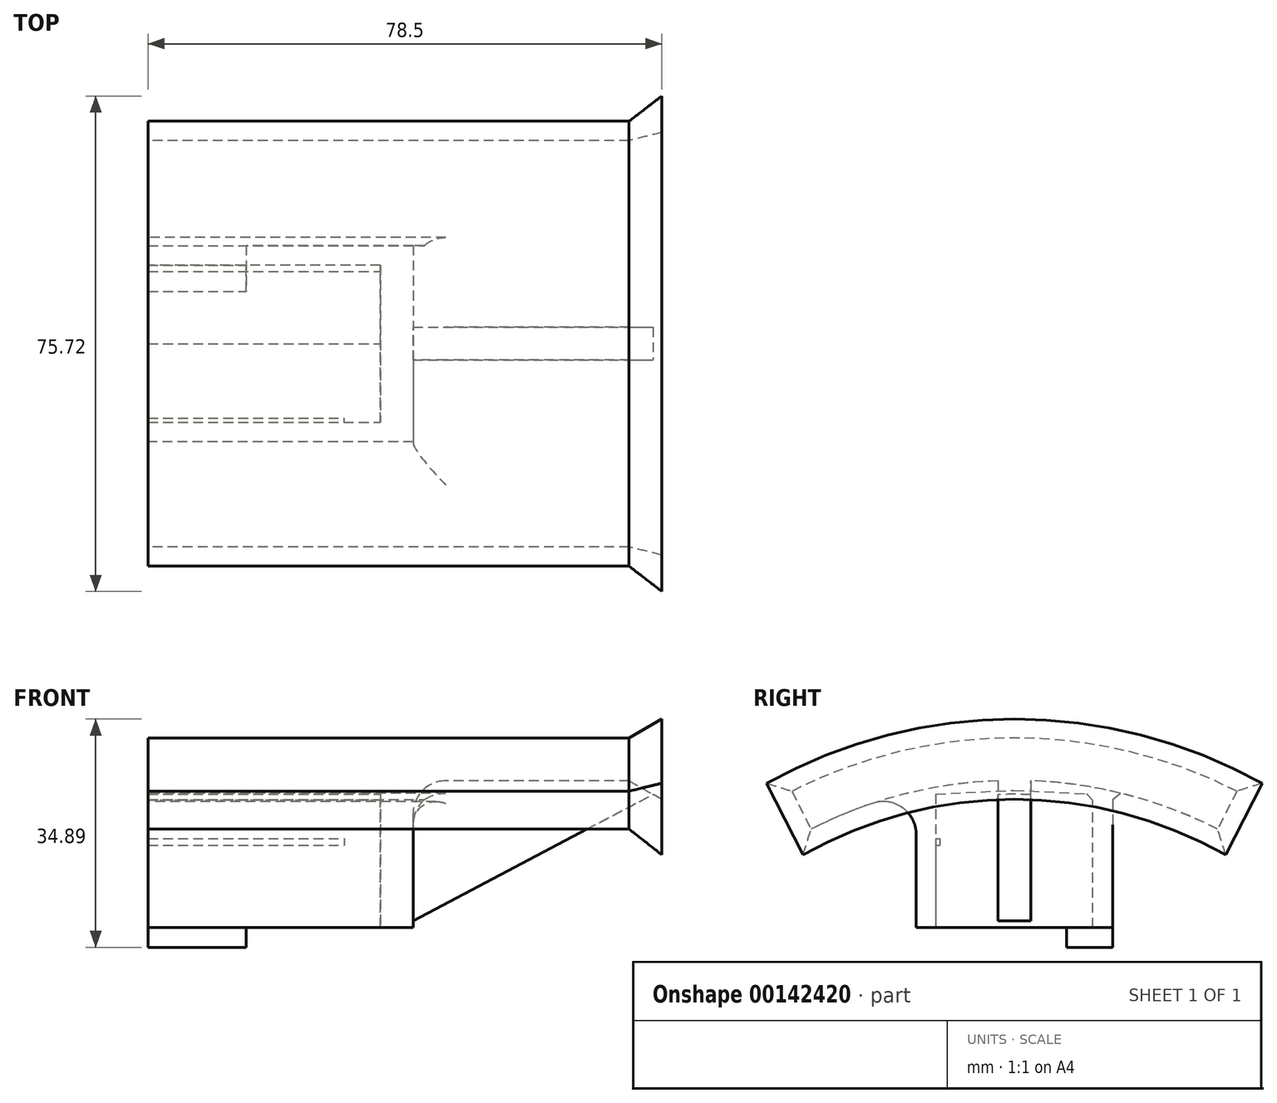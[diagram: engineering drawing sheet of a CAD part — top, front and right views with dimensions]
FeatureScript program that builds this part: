
annotation { "Feature Type Name" : "Feature", "Feature Type Description" : "" }
export const myFeature = defineFeature(function(context is Context, id is Id, definition is map)
    precondition{}
    {
        {
            var Q0;
            Q0=qCreatedBy(makeId("Right.planeOp"),FACE);
            var sketch = newSketch(context, id + "F0", { "sketchPlane" : qUnion([Q0])});
            skLineSegment(sketch, "E0", {"start": v(0, 0) * mm, "end": v(0, -27) * mm});
            skLineSegment(sketch, "E1", {"start": v(0, -27) * mm, "end": v(-7, -27) * mm});
            skLineSegment(sketch, "E2", {"start": v(-7, -27) * mm, "end": v(-7, -24) * mm});
            skLineSegment(sketch, "E3", {"start": v(-7, -24) * mm, "end": v(-3, -24) * mm});
            skLineSegment(sketch, "E4", {"start": v(-3, -24) * mm, "end": v(-3, -3) * mm});
            skLineSegment(sketch, "E5", {"start": v(-3, -3) * mm, "end": v(-27, -3) * mm});
            skLineSegment(sketch, "E6", {"start": v(-27, -3) * mm, "end": v(-27, -24) * mm});
            skLineSegment(sketch, "E7", {"start": v(-27, -24) * mm, "end": v(-30, -24) * mm});
            skLineSegment(sketch, "E8", {"start": v(-30, -24) * mm, "end": v(-30, 0) * mm});
            skLineSegment(sketch, "E9", {"start": v(-30, 0) * mm, "end": v(0, 0) * mm});
            skLineSegment(sketch, "E10.bottom", {"start": v(-27, -10.4) * mm, "end": v(-26.4, -10.4) * mm});
            skLineSegment(sketch, "E10.top", {"start": v(-27, -11.4) * mm, "end": v(-26.4, -11.4) * mm});
            skLineSegment(sketch, "E10.left", {"start": v(-27, -10.4) * mm, "end": v(-27, -11.4) * mm});
            skLineSegment(sketch, "E10.right", {"start": v(-26.4, -10.4) * mm, "end": v(-26.4, -11.4) * mm});
            skLineSegment(sketch, "E11", {"start": v(-3, -24) * mm, "end": v(0, -24) * mm});
            skLineSegment(sketch, "E12", {"start": v(-27, -3.6) * mm, "end": v(-15, -3) * mm});
            skLineSegment(sketch, "E13", {"start": v(-15, -3) * mm, "end": v(-3, -3.6) * mm});
            skSolve(sketch);
        }
        {
            var Q0;
            Q0=makeQuery(id+"F0.imprint","IMPRINT",FACE,{"disambiguationData":[TD([[makeQuery(id+"F0.imprint","IMPRINT",EDGE,{"derivedFrom":sQuery(id+"F0.wireOp",EDGE,"E0")}),-1.0]])]});
            var Q1;
            Q1=makeQuery(id+"F0.imprint","IMPRINT",FACE,{"disambiguationData":[TD([[makeQuery(id+"F0.imprint","IMPRINT",EDGE,{"derivedFrom":sQuery(id+"F0.wireOp",EDGE,"E10.bottom")}),-1.0]])]});
            var Q2;
            Q2=makeQuery(id+"F0.imprint","IMPRINT",FACE,{"disambiguationData":[TD([[makeQuery(id+"F0.imprint","IMPRINT",EDGE,{"derivedFrom":sQuery(id+"F0.wireOp",EDGE,"E4")}),-1.0]])]});
            var Q3;
            {var subQ3=sQuery(id+"F0.wireOp",EDGE,"E13");Q3=makeQuery(id+"F0.imprint","IMPRINT",FACE,{"disambiguationData":[TD([[makeQuery(id+"F0.imprint","IMPRINT",EDGE,{"derivedFrom":subQ3}),1.0]])]});}
            var Q4;
            {var subQ3=sQuery(id+"F0.wireOp",EDGE,"E12");Q4=makeQuery(id+"F0.imprint","IMPRINT",FACE,{"disambiguationData":[TD([[makeQuery(id+"F0.imprint","IMPRINT",EDGE,{"derivedFrom":subQ3}),1.0]])]});}
            extrude(context, id + "F1", {"entities" : qUnion([Q0, Q1, Q2, Q3, Q4]), "oppositeDirection" : true, "depth" : 15 * mm});
        }
        {
            var Q0;
            Q0=makeQuery(id+"F1.opExtrude","CAP_FACE",FACE,{"disambiguationData":[OSD([sQuery(id+"F0.wireOp",EDGE,"E0"),sQuery(id+"F0.wireOp",EDGE,"E1"),sQuery(id+"F0.wireOp",EDGE,"E2"),sQuery(id+"F0.wireOp",EDGE,"E3"),sQuery(id+"F0.wireOp",EDGE,"E4"),sQuery(id+"F0.wireOp",EDGE,"E5"),sQuery(id+"F0.wireOp",EDGE,"E6"),sQuery(id+"F0.wireOp",EDGE,"E7"),sQuery(id+"F0.wireOp",EDGE,"E8"),sQuery(id+"F0.wireOp",EDGE,"E9"),sQuery(id+"F0.wireOp",EDGE,"E10.bottom"),sQuery(id+"F0.wireOp",EDGE,"E10.top"),sQuery(id+"F0.wireOp",EDGE,"E10.right")])],"isStart":true});
            var sketch = newSketch(context, id + "F2", { "sketchPlane" : qUnion([Q0])});
            skLineSegment(sketch, "E14.bottom", {"start": v(-30, 0) * mm, "end": v(-27, 0) * mm});
            skLineSegment(sketch, "E14.top", {"start": v(-30, -24) * mm, "end": v(-27, -24) * mm});
            skLineSegment(sketch, "E14.left", {"start": v(-30, 0) * mm, "end": v(-30, -24) * mm});
            skLineSegment(sketch, "E14.right", {"start": v(-27, 0) * mm, "end": v(-27, -24) * mm});
            skLineSegment(sketch, "E15.bottom", {"start": v(0, 0) * mm, "end": v(-27, 0) * mm});
            skLineSegment(sketch, "E15.top", {"start": v(0, -24) * mm, "end": v(-27, -24) * mm});
            skLineSegment(sketch, "E15.left", {"start": v(0, 0) * mm, "end": v(0, -24) * mm});
            skLineSegment(sketch, "E16.bottom", {"start": v(0, -24) * mm, "end": v(-3, -24) * mm});
            skLineSegment(sketch, "E16.top", {"start": v(0, -24) * mm, "end": v(-3, -24) * mm});
            skLineSegment(sketch, "E16.left", {"start": v(0, -24) * mm, "end": v(0, -24) * mm});
            skLineSegment(sketch, "E16.right", {"start": v(-3, -24) * mm, "end": v(-3, -24) * mm});
            skSolve(sketch);
        }
        {
            var Q0;
            Q0=makeQuery(id+"F2.imprint","IMPRINT",FACE,{"disambiguationData":[TD([[makeQuery(id+"F2.imprint","IMPRINT",EDGE,{"derivedFrom":sQuery(id+"F2.wireOp",EDGE,"E14.bottom")}),-1.0]])]});
            var Q1;
            Q1=makeQuery(id+"F2.imprint","IMPRINT",FACE,{"disambiguationData":[TD([[makeQuery(id+"F2.imprint","IMPRINT",EDGE,{"derivedFrom":sQuery(id+"F2.wireOp",EDGE,"E15.bottom")}),-1.0]])]});
            extrude(context, id + "F3", {"entities" : qUnion([Q0, Q1]), "operationType" : NewBodyOperationType.ADD, "depth" : 20.5 * mm});
        }
        {
            var Q0;
            Q0=makeQuery(id+"F3.opExtrude","CAP_FACE",FACE,{"disambiguationData":[OSD([sQuery(id+"F2.wireOp",EDGE,"E14.bottom"),sQuery(id+"F2.wireOp",EDGE,"E14.top"),sQuery(id+"F2.wireOp",EDGE,"E14.left"),sQuery(id+"F2.wireOp",EDGE,"E14.right"),sQuery(id+"F2.wireOp",EDGE,"E15.bottom"),sQuery(id+"F2.wireOp",EDGE,"E15.top"),sQuery(id+"F2.wireOp",EDGE,"E15.left"),sQuery(id+"F2.wireOp",EDGE,"E16.bottom")])],"isStart":false});
            var sketch = newSketch(context, id + "F4", { "sketchPlane" : qUnion([Q0])});
            skLineSegment(sketch, "E17.bottom", {"start": v(-30, 0) * mm, "end": v(0, 0) * mm});
            skLineSegment(sketch, "E17.top", {"start": v(-30, -24) * mm, "end": v(0, -24) * mm});
            skLineSegment(sketch, "E17.left", {"start": v(-30, 0) * mm, "end": v(-30, -24) * mm});
            skLineSegment(sketch, "E17.right", {"start": v(0, 0) * mm, "end": v(0, -24) * mm});
            skSolve(sketch);
        }
        {
            var Q0;
            Q0=qSketchRegion(id+"F4",true);
            extrude(context, id + "F5", {"entities" : qUnion([Q0]), "operationType" : NewBodyOperationType.ADD, "depth" : 5 * mm});
        }
        {
            var Q0;
            Q0=makeQuery(id+"F5.opExtrude","CAP_FACE",FACE,{"disambiguationData":[OSD([sQuery(id+"F4.wireOp",EDGE,"E17.bottom"),sQuery(id+"F4.wireOp",EDGE,"E17.top"),sQuery(id+"F4.wireOp",EDGE,"E17.left"),sQuery(id+"F4.wireOp",EDGE,"E17.right")])],"isStart":false});
            var sketch = newSketch(context, id + "F6", { "sketchPlane" : qUnion([Q0])});
            skCircle(sketch, "E18", {"center": v(-15, -70) * mm, "radius": 75 * mm});
            skCircle(sketch, "E19", {"center": v(-15, -70) * mm, "radius": 68.5 * mm});
            skLineSegment(sketch, "E20", {"start": v(-49, -3.15) * mm, "end": v(-15, -70) * mm});
            skLineSegment(sketch, "E21", {"start": v(19, -3.15) * mm, "end": v(-15, -70) * mm});
            skSolve(sketch);
        }
        {
            var Q0;
            {var subQ12=makeQuery(id+"F5.opExtrude","CAP_EDGE",EDGE,{"disambiguationData":[OSD([sQuery(id+"F4.wireOp",EDGE,"E17.bottom")])],"isStart":false});Q0=makeQuery(id+"F6.imprint","IMPRINT",FACE,{"disambiguationData":[TD([[makeQuery(id+"F6.imprint","IMPRINT",EDGE,{"derivedFrom":subQ12}),1.0]])]});}
            var Q1;
            {var subQ5=makeQuery(id+"F5.opExtrude","CAP_EDGE",EDGE,{"disambiguationData":[OSD([sQuery(id+"F4.wireOp",EDGE,"E17.bottom")])],"isStart":false});Q1=makeQuery(id+"F6.imprint","IMPRINT",FACE,{"disambiguationData":[TD([[makeQuery(id+"F6.imprint","IMPRINT",EDGE,{"derivedFrom":subQ5}),-1.0]])]});}
            var Q2;
            Q2=makeQuery(id+"F1.opExtrude","CAP_FACE",FACE,{"disambiguationData":[OSD([sQuery(id+"F0.wireOp",EDGE,"E0"),sQuery(id+"F0.wireOp",EDGE,"E1"),sQuery(id+"F0.wireOp",EDGE,"E2"),sQuery(id+"F0.wireOp",EDGE,"E3"),sQuery(id+"F0.wireOp",EDGE,"E4"),sQuery(id+"F0.wireOp",EDGE,"E5"),sQuery(id+"F0.wireOp",EDGE,"E6"),sQuery(id+"F0.wireOp",EDGE,"E7"),sQuery(id+"F0.wireOp",EDGE,"E8"),sQuery(id+"F0.wireOp",EDGE,"E9"),sQuery(id+"F0.wireOp",EDGE,"E10.bottom"),sQuery(id+"F0.wireOp",EDGE,"E10.top"),sQuery(id+"F0.wireOp",EDGE,"E10.right")])],"isStart":false});
            extrude(context, id + "F7", {"entities" : qUnion([Q0, Q1]), "operationType" : NewBodyOperationType.ADD, "depth" : 33 * mm, "hasSecondDirection" : true, "secondDirectionBound" : SecondDirectionBoundingType.UP_TO_SURFACE, "secondDirectionOppositeDirection" : true, "secondDirectionBoundEntityFace" : qUnion([Q2]), "secondDirectionDepth" : 25 * mm});
        }
        {
            var Q0;
            Q0=makeQuery(id+"F7.opExtrude","CAP_FACE",FACE,{"disambiguationData":[OSD([sQuery(id+"F6.wireOp",EDGE,"E18"),sQuery(id+"F6.wireOp",EDGE,"E19"),sQuery(id+"F6.wireOp",EDGE,"E20"),sQuery(id+"F6.wireOp",EDGE,"E21")])],"isStart":false});
            extrude(context, id + "F8", {"entities" : qUnion([Q0]), "operationType" : NewBodyOperationType.ADD, "depth" : 5 * mm, "hasDraft" : true, "draftAngle" : 30 * degree});
        }
        {
            var Q0;
            Q0=qCreatedBy(makeId("Front.planeOp"),FACE);
            var sketch = newSketch(context, id + "F9", { "sketchPlane" : qUnion([Q0])});
            skLineSegment(sketch, "E22", {"start": v(25.49, -22.98) * mm, "end": v(63.38, -2.98) * mm});
            skLineSegment(sketch, "E23", {"start": v(63.38, -2.98) * mm, "end": v(63.38, 0.02) * mm});
            skLineSegment(sketch, "E24", {"start": v(63.38, 0.02) * mm, "end": v(25.5, 0.02) * mm});
            skLineSegment(sketch, "E25", {"start": v(25.5, 0.02) * mm, "end": v(25.49, -22.98) * mm});
            skSolve(sketch);
        }
        {
            var Q0;
            Q0=qSketchRegion(id+"F9",true);
            extrude(context, id + "F10", {"entities" : qUnion([Q0]), "depth" : 5 * mm});
        }
        {
            var Q0;
            Q0=makeQuery(id+"F10.opExtrude","SWEPT_BODY",BODY,{"disambiguationData":[OSD([sQuery(id+"F9.wireOp",EDGE,"E22"),sQuery(id+"F9.wireOp",EDGE,"E23"),sQuery(id+"F9.wireOp",EDGE,"E24"),sQuery(id+"F9.wireOp",EDGE,"E25")])]});
            var Q1;
            Q1=makeQuery(id+"F5.opExtrude","CAP_EDGE",EDGE,{"disambiguationData":[OSD([sQuery(id+"F4.wireOp",EDGE,"E17.top")])],"isStart":false});
            transform(context, id + "F11", {"entities" : qUnion([Q0]), "transformType" : TransformType.TRANSLATION_DISTANCE, "transformDirection" : qUnion([Q1]), "distance" : 12.5 * mm, "makeCopy" : false});
        }
        {
            var Q0;
            Q0=makeQuery(id+"F10.opExtrude","SWEPT_BODY",BODY,{"disambiguationData":[OSD([sQuery(id+"F9.wireOp",EDGE,"E22"),sQuery(id+"F9.wireOp",EDGE,"E23"),sQuery(id+"F9.wireOp",EDGE,"E24"),sQuery(id+"F9.wireOp",EDGE,"E25")])]});
            var Q1;
            Q1=makeQuery(id+"F1.opExtrude","SWEPT_BODY",BODY,{"disambiguationData":[OSD([sQuery(id+"F0.wireOp",EDGE,"E0"),sQuery(id+"F0.wireOp",EDGE,"E1"),sQuery(id+"F0.wireOp",EDGE,"E2"),sQuery(id+"F0.wireOp",EDGE,"E3"),sQuery(id+"F0.wireOp",EDGE,"E4"),sQuery(id+"F0.wireOp",EDGE,"E5"),sQuery(id+"F0.wireOp",EDGE,"E6"),sQuery(id+"F0.wireOp",EDGE,"E7"),sQuery(id+"F0.wireOp",EDGE,"E8"),sQuery(id+"F0.wireOp",EDGE,"E9"),sQuery(id+"F0.wireOp",EDGE,"E10.bottom"),sQuery(id+"F0.wireOp",EDGE,"E10.top"),sQuery(id+"F0.wireOp",EDGE,"E10.right")])]});
            booleanBodies(context, id + "F12", {"operationType" : BooleanOperationType.UNION, "tools" : qUnion([Q0, Q1])});
        }
        {
            var Q0;
            Q0=makeQuery(id+"F7.boolean.opBoolean","INTERSECT",EDGE,{"derivedFrom":[makeQuery(id+"F5.boolean.opBoolean","MERGE",FACE,{"derivedFrom":[makeQuery(id+"F3.boolean.opBoolean","MERGE",FACE,{"derivedFrom":[makeQuery(id+"F1.opExtrude","SWEPT_FACE",FACE,{"disambiguationData":[OSD([sQuery(id+"F0.wireOp",EDGE,"E8")])]}),makeQuery(id+"F3.opExtrude","SWEPT_FACE",FACE,{"disambiguationData":[OSD([sQuery(id+"F2.wireOp",EDGE,"E14.left")])]})]}),makeQuery(id+"F5.opExtrude","SWEPT_FACE",FACE,{"disambiguationData":[OSD([sQuery(id+"F4.wireOp",EDGE,"E17.left")])]})]}),makeQuery(id+"F7.opExtrude","SWEPT_FACE",FACE,{"disambiguationData":[OSD([sQuery(id+"F6.wireOp",EDGE,"E19")])]})]});
            var Q1;
            {var subQ0=sQuery(id+"F4.wireOp",EDGE,"E17.right");var subQ1=makeQuery(id+"F5.opExtrude","CAP_FACE",FACE,{"disambiguationData":[OSD([sQuery(id+"F4.wireOp",EDGE,"E17.bottom"),sQuery(id+"F4.wireOp",EDGE,"E17.top"),sQuery(id+"F4.wireOp",EDGE,"E17.left"),subQ0])],"isStart":false});var subQ2=makeQuery(id+"F7.opExtrude","SWEPT_FACE",FACE,{"disambiguationData":[OSD([sQuery(id+"F6.wireOp",EDGE,"E19")])]});Q1=makeQuery(id+"F12.opBoolean","SPLIT",EDGE,{"disambiguationData":[TD([makeQuery(id+"F1.opExtrude","SWEPT_FACE",FACE,{"disambiguationData":[OSD([sQuery(id+"F0.wireOp",EDGE,"E0")])]})])],"derivedFrom":makeQuery(id+"F7.boolean.opBoolean","INTERSECT",EDGE,{"derivedFrom":[subQ1,subQ2]})});}
            var Q2;
            {var subQ0=sQuery(id+"F4.wireOp",EDGE,"E17.left");var subQ1=makeQuery(id+"F5.opExtrude","CAP_FACE",FACE,{"disambiguationData":[OSD([sQuery(id+"F4.wireOp",EDGE,"E17.bottom"),sQuery(id+"F4.wireOp",EDGE,"E17.top"),subQ0,sQuery(id+"F4.wireOp",EDGE,"E17.right")])],"isStart":false});var subQ2=makeQuery(id+"F7.opExtrude","SWEPT_FACE",FACE,{"disambiguationData":[OSD([sQuery(id+"F6.wireOp",EDGE,"E19")])]});Q2=makeQuery(id+"F12.opBoolean","SPLIT",EDGE,{"disambiguationData":[TD([makeQuery(id+"F1.opExtrude","SWEPT_FACE",FACE,{"disambiguationData":[OSD([sQuery(id+"F0.wireOp",EDGE,"E8")])]})])],"derivedFrom":makeQuery(id+"F7.boolean.opBoolean","INTERSECT",EDGE,{"derivedFrom":[subQ1,subQ2]})});}
            fillet(context, id + "F13", {"entities" : qUnion([Q0, Q1, Q2]), "radius" : 5 * mm, "tangentPropagation" : true, "allowEdgeOverflow" : false});
        }
        {
            var Q0;
            Q0=makeQuery(id+"F7.boolean.opBoolean","INTERSECT",EDGE,{"derivedFrom":[makeQuery(id+"F5.boolean.opBoolean","MERGE",FACE,{"derivedFrom":[makeQuery(id+"F3.boolean.opBoolean","MERGE",FACE,{"derivedFrom":[makeQuery(id+"F1.opExtrude","SWEPT_FACE",FACE,{"disambiguationData":[OSD([sQuery(id+"F0.wireOp",EDGE,"E0")])]}),makeQuery(id+"F3.opExtrude","SWEPT_FACE",FACE,{"disambiguationData":[OSD([sQuery(id+"F2.wireOp",EDGE,"E15.left")])]})]}),makeQuery(id+"F5.opExtrude","SWEPT_FACE",FACE,{"disambiguationData":[OSD([sQuery(id+"F4.wireOp",EDGE,"E17.right")])]})]}),makeQuery(id+"F7.opExtrude","SWEPT_FACE",FACE,{"disambiguationData":[OSD([sQuery(id+"F6.wireOp",EDGE,"E19")])]})]});
            chamfer(context, id + "F14", {"entities" : qUnion([Q0]), "width" : 1 * mm, "tangentPropagation" : true});
        }
        {
            var Q0;
            Q0=makeQuery(id+"FxV5dlsvzGUwSKC_2.boolean.opBoolean","MERGE",EDGE,{"derivedFrom":[makeQuery(id+"F1.opExtrude","SWEPT_EDGE",EDGE,{"disambiguationData":[OSD([sQuery(id+"F0.wireOp",EDGE,"E4"),sQuery(id+"F0.wireOp",EDGE,"E5")])]}),makeQuery(id+"FxV5dlsvzGUwSKC_2.opExtrude","SWEPT_EDGE",EDGE,{"disambiguationData":[OSD([sQuery(id+"FTIyNGWiZXPathp_2.wireOp",EDGE,"jA4ZDa5l-lHbp-5HIl-XP0d-kzFAkvVPCaqd.top"),sQuery(id+"FTIyNGWiZXPathp_2.wireOp",EDGE,"jA4ZDa5l-lHbp-5HIl-XP0d-kzFAkvVPCaqd.left")])]})]});
            chamfer(context, id + "F15", {"entities" : qUnion([Q0]), "width" : 1 * mm, "tangentPropagation" : true});
        }
        {
            var Q0;
            {var subQ0=sQuery(id+"F0.wireOp",EDGE,"E7");var subQ1=sQuery(id+"F0.wireOp",EDGE,"E6");var subQ3=sQuery(id+"F0.wireOp",EDGE,"E10.top");var subQ4=sQuery(id+"F0.wireOp",EDGE,"E10.bottom");var subQ5=sQuery(id+"F0.wireOp",EDGE,"E12");var subQ6=sQuery(id+"F0.wireOp",EDGE,"E10.right");Q0=makeQuery(id+"F3.boolean.opBoolean","SPLIT",FACE,{"disambiguationData":[TD([makeQuery(id+"F1.opExtrude","SWEPT_FACE",FACE,{"disambiguationData":[OSD([subQ4])]})])],"derivedFrom":makeQuery(id+"F1.opExtrude","CAP_FACE",FACE,{"disambiguationData":[OSD([sQuery(id+"F0.wireOp",EDGE,"E0"),sQuery(id+"F0.wireOp",EDGE,"E1"),sQuery(id+"F0.wireOp",EDGE,"E2"),sQuery(id+"F0.wireOp",EDGE,"E3"),sQuery(id+"F0.wireOp",EDGE,"E4"),subQ1,subQ0,sQuery(id+"F0.wireOp",EDGE,"E8"),sQuery(id+"F0.wireOp",EDGE,"E9"),subQ4,subQ3,subQ6,subQ5,sQuery(id+"F0.wireOp",EDGE,"E13")])],"isStart":true})});}
            extrude(context, id + "F16", {"entities" : qUnion([Q0]), "operationType" : NewBodyOperationType.ADD, "depth" : 15 * mm});
        }
    });
